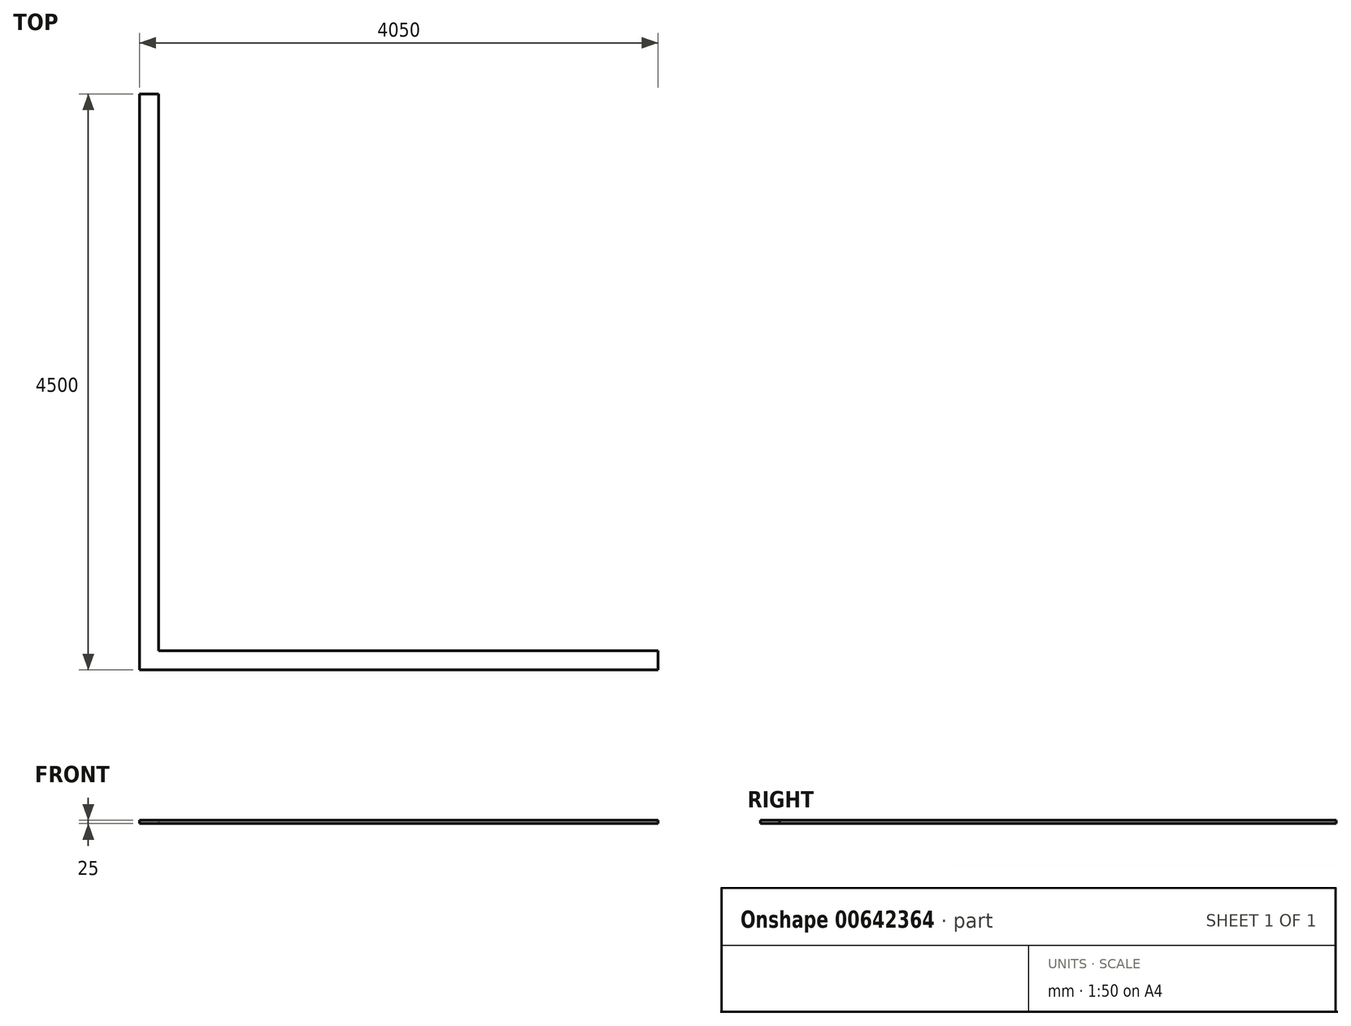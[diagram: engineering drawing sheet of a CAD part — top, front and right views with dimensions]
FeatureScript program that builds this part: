
annotation { "Feature Type Name" : "Feature", "Feature Type Description" : "" }
export const myFeature = defineFeature(function(context is Context, id is Id, definition is map)
    precondition{}
    {
        {
            var Q0;
            Q0=qCreatedBy(makeId("Top.planeOp"),FACE);
            var sketch = newSketch(context, id + "F0", { "sketchPlane" : qUnion([Q0])});
            skLineSegment(sketch, "E0", {"start": v(0, 0) * mm, "end": v(4050, 0) * mm});
            skLineSegment(sketch, "E1", {"start": v(0, 0) * mm, "end": v(0, 4500) * mm});
            skLineSegment(sketch, "E2.0", {"start": v(150, 150) * mm, "end": v(4050, 150) * mm});
            skLineSegment(sketch, "E2.1", {"start": v(150, 150) * mm, "end": v(150, 4500) * mm});
            skLineSegment(sketch, "E3", {"start": v(4050, 150) * mm, "end": v(4050, 0) * mm});
            skLineSegment(sketch, "E4", {"start": v(0, 4500) * mm, "end": v(150, 4500) * mm});
            skSolve(sketch);
        }
        {
            var Q0;
            Q0=makeQuery(id+"F0.imprint","IMPRINT",FACE,{"disambiguationData":[TD([[makeQuery(id+"F0.imprint","IMPRINT",EDGE,{"derivedFrom":sQuery(id+"F0.wireOp",EDGE,"E0")}),1.0]])]});
            extrude(context, id + "F1", {"entities" : qUnion([Q0]), "depth" : 25 * mm, "offsetDistance" : 25 * mm});
        }
    });
